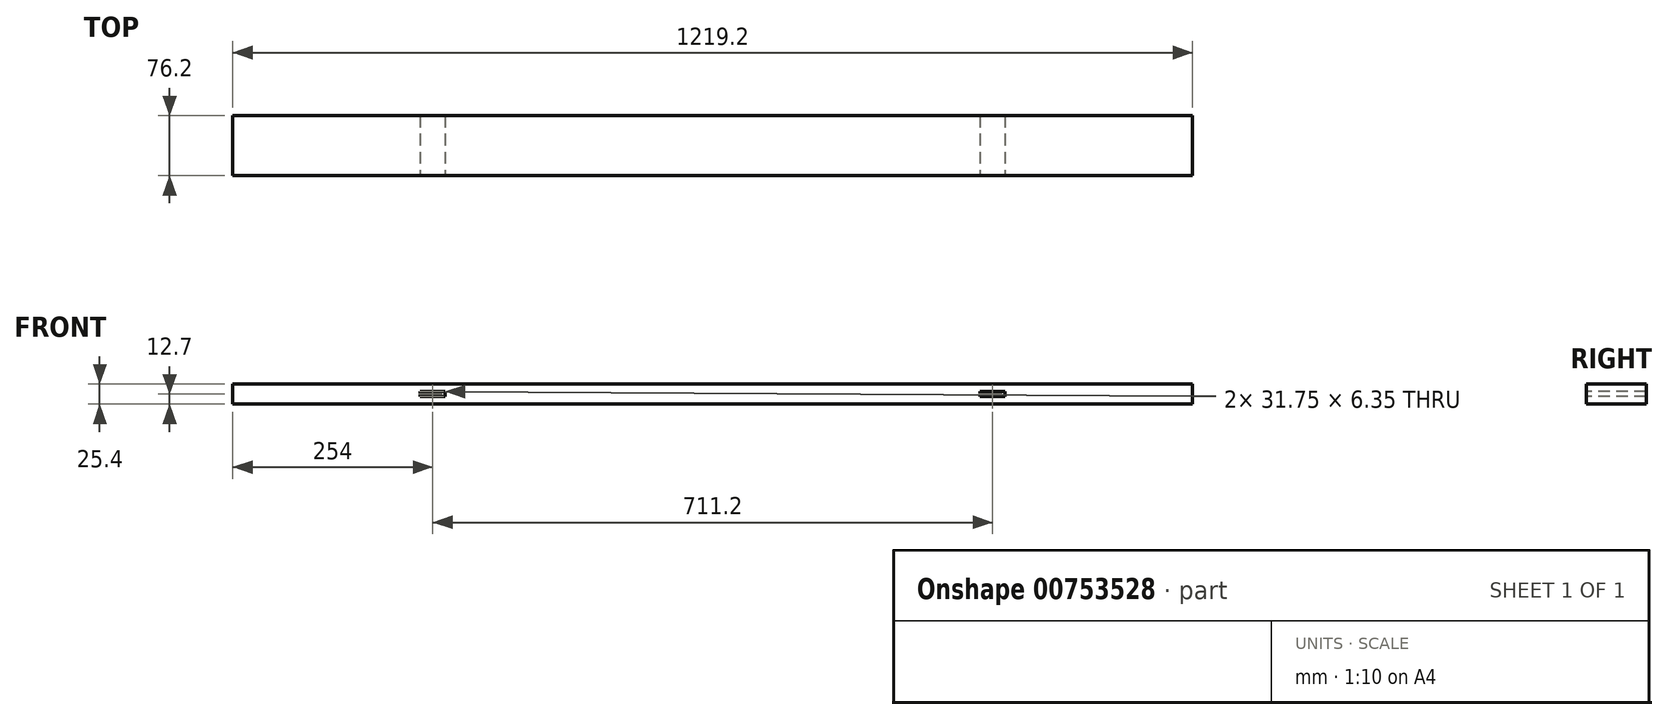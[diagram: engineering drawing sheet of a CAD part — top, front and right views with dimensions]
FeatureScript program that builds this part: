
annotation { "Feature Type Name" : "Feature", "Feature Type Description" : "" }
export const myFeature = defineFeature(function(context is Context, id is Id, definition is map)
    precondition{}
    {
        {
            var Q0;
            Q0=qCreatedBy(makeId("Top.planeOp"),FACE);
            var sketch = newSketch(context, id + "F0", { "sketchPlane" : qUnion([Q0])});
            skLineSegment(sketch, "E0.bottom", {"start": v(609.6, -38.1) * mm, "end": v(-609.6, -38.1) * mm});
            skLineSegment(sketch, "E0.top", {"start": v(609.6, 38.1) * mm, "end": v(-609.6, 38.1) * mm});
            skLineSegment(sketch, "E0.left", {"start": v(609.6, -38.1) * mm, "end": v(609.6, 38.1) * mm});
            skLineSegment(sketch, "E0.right", {"start": v(-609.6, -38.1) * mm, "end": v(-609.6, 38.1) * mm});
            skPoint(sketch, "E0.middle", {"position": v(0, 0) * mm});
            skSolve(sketch);
        }
        {
            var Q0;
            Q0=makeQuery(id+"F0.imprint","IMPRINT",FACE,{"disambiguationData":[TD([[makeQuery(id+"F0.imprint","IMPRINT",EDGE,{"derivedFrom":sQuery(id+"F0.wireOp",EDGE,"E0.bottom")}),-1.0]])]});
            extrude(context, id + "F1", {"entities" : qUnion([Q0]), "endBound" : BoundingType.SYMMETRIC, "depth" : 25.4 * mm, "offsetDistance" : 25.4 * mm});
        }
        {
            var Q0;
            Q0=makeQuery(id+"F1.opExtrude","SWEPT_FACE",FACE,{"disambiguationData":[OSD([sQuery(id+"F0.wireOp",EDGE,"E0.bottom")])]});
            var sketch = newSketch(context, id + "F2", { "sketchPlane" : qUnion([Q0])});
            skLineSegment(sketch, "E1.bottom", {"start": v(-339.73, 3.17) * mm, "end": v(-371.48, 3.17) * mm});
            skLineSegment(sketch, "E1.top", {"start": v(-339.73, -3.18) * mm, "end": v(-371.48, -3.18) * mm});
            skLineSegment(sketch, "E1.left", {"start": v(-339.73, 3.17) * mm, "end": v(-339.73, -3.18) * mm});
            skLineSegment(sketch, "E1.right", {"start": v(-371.48, 3.17) * mm, "end": v(-371.48, -3.18) * mm});
            skPoint(sketch, "E1.middle", {"position": v(-355.6, 0) * mm});
            skLineSegment(sketch, "E2.MirrorCS", {"start": v(339.73, 3.17) * mm, "end": v(371.48, 3.17) * mm});
            skLineSegment(sketch, "E3.MirrorCS", {"start": v(371.48, 3.17) * mm, "end": v(371.48, -3.18) * mm});
            skLineSegment(sketch, "E4.MirrorCS", {"start": v(339.73, -3.18) * mm, "end": v(371.48, -3.18) * mm});
            skLineSegment(sketch, "E5.MirrorCS", {"start": v(339.73, 3.17) * mm, "end": v(339.73, -3.18) * mm});
            skSolve(sketch);
        }
        {
            var Q0;
            Q0=makeQuery(id+"F2.imprint","IMPRINT",FACE,{"disambiguationData":[TD([[makeQuery(id+"F2.imprint","IMPRINT",EDGE,{"derivedFrom":sQuery(id+"F2.wireOp",EDGE,"E1.bottom")}),1.0]])]});
            extrude(context, id + "F3", {"entities" : qUnion([Q0]), "operationType" : NewBodyOperationType.REMOVE, "endBound" : BoundingType.UP_TO_NEXT, "oppositeDirection" : true, "depth" : 25.4 * mm, "offsetDistance" : 25.4 * mm});
        }
        {
            var Q0;
            Q0=makeQuery(id+"F2.imprint","IMPRINT",FACE,{"disambiguationData":[TD([[makeQuery(id+"F2.imprint","IMPRINT",EDGE,{"derivedFrom":sQuery(id+"F2.wireOp",EDGE,"E2.MirrorCS")}),-1.0]])]});
            extrude(context, id + "F4", {"entities" : qUnion([Q0]), "operationType" : NewBodyOperationType.REMOVE, "endBound" : BoundingType.UP_TO_NEXT, "oppositeDirection" : true, "depth" : 25.4 * mm, "offsetDistance" : 25.4 * mm});
        }
    });
